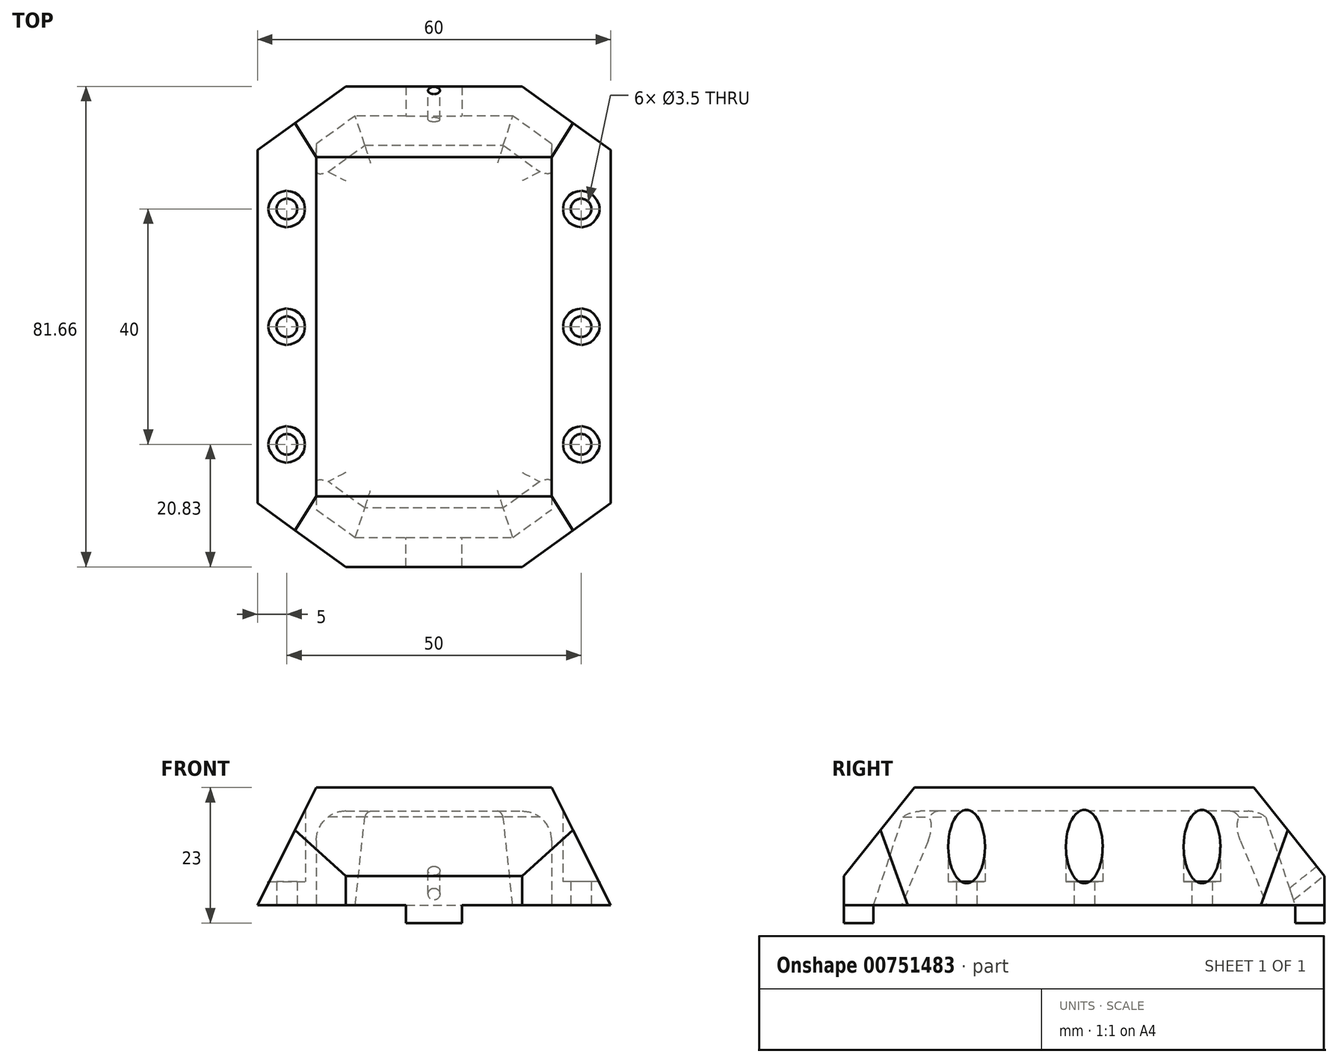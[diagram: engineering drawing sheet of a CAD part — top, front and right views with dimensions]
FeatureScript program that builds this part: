
annotation { "Feature Type Name" : "Feature", "Feature Type Description" : "" }
export const myFeature = defineFeature(function(context is Context, id is Id, definition is map)
    precondition{}
    {
        {
            var Q0;
            Q0=qCreatedBy(makeId("Top.planeOp"),FACE);
            var sketch = newSketch(context, id + "F0", { "sketchPlane" : qUnion([Q0])});
            skCircle(sketch, "E0", {"center": v(-25, 20) * mm, "radius": 1.75 * mm});
            skCircle(sketch, "E1", {"center": v(-25, 0) * mm, "radius": 1.75 * mm});
            skCircle(sketch, "E2", {"center": v(-25, -20) * mm, "radius": 1.75 * mm});
            skCircle(sketch, "E3", {"center": v(25, 20) * mm, "radius": 1.75 * mm});
            skCircle(sketch, "E4", {"center": v(25, 0) * mm, "radius": 1.75 * mm});
            skCircle(sketch, "E5", {"center": v(25, -20) * mm, "radius": 1.75 * mm});
            skLineSegment(sketch, "E6", {"start": v(-25, 0) * mm, "end": v(-25, 20) * mm, "construction": true});
            skLineSegment(sketch, "E7", {"start": v(-25, 0) * mm, "end": v(-25, -20) * mm, "construction": true});
            skLineSegment(sketch, "E8", {"start": v(-30, 30) * mm, "end": v(-30, -30) * mm});
            skPoint(sketch, "E9", {"position": v(-30, 0) * mm});
            skLineSegment(sketch, "E10", {"start": v(-30, 30) * mm, "end": v(-15, 40.83) * mm});
            skLineSegment(sketch, "E11.MirrorCS", {"start": v(-30, -30) * mm, "end": v(-15, -40.83) * mm});
            skLineSegment(sketch, "E12.MirrorCS", {"start": v(30, 30) * mm, "end": v(15, 40.83) * mm});
            skLineSegment(sketch, "E13.MirrorCS", {"start": v(30, 30) * mm, "end": v(30, -30) * mm});
            skLineSegment(sketch, "E14.MirrorCS", {"start": v(30, -30) * mm, "end": v(15, -40.83) * mm});
            skLineSegment(sketch, "E15", {"start": v(-15, 40.83) * mm, "end": v(15, 40.83) * mm});
            skLineSegment(sketch, "E16", {"start": v(-15, -40.83) * mm, "end": v(15, -40.83) * mm});
            skLineSegment(sketch, "E17.0", {"start": v(-20, -24.89) * mm, "end": v(-11.77, -30.83) * mm});
            skLineSegment(sketch, "E17.1", {"start": v(-20, 24.89) * mm, "end": v(-20, -24.89) * mm});
            skLineSegment(sketch, "E17.2", {"start": v(-11.77, -30.83) * mm, "end": v(11.77, -30.83) * mm});
            skLineSegment(sketch, "E17.3", {"start": v(-20, 24.89) * mm, "end": v(-11.77, 30.83) * mm});
            skLineSegment(sketch, "E17.4", {"start": v(20, -24.89) * mm, "end": v(11.77, -30.83) * mm});
            skLineSegment(sketch, "E17.5", {"start": v(20, 24.89) * mm, "end": v(20, -24.89) * mm});
            skLineSegment(sketch, "E17.6", {"start": v(20, 24.89) * mm, "end": v(11.77, 30.83) * mm});
            skLineSegment(sketch, "E17.7", {"start": v(-11.77, 30.83) * mm, "end": v(11.77, 30.83) * mm});
            skCircle(sketch, "E18", {"center": v(-25, -20) * mm, "radius": 3.12 * mm});
            skCircle(sketch, "E19", {"center": v(-25, 0) * mm, "radius": 3.12 * mm});
            skCircle(sketch, "E20", {"center": v(-25, 20) * mm, "radius": 3.12 * mm});
            skCircle(sketch, "E21.MirrorC", {"center": v(25, 20) * mm, "radius": 3.12 * mm});
            skCircle(sketch, "E22.MirrorC", {"center": v(25, 0) * mm, "radius": 3.12 * mm});
            skCircle(sketch, "E23.MirrorC", {"center": v(25, -20) * mm, "radius": 3.12 * mm});
            skSolve(sketch);
        }
        {
            var Q0;
            Q0=makeQuery(id+"F0.imprint","IMPRINT",FACE,{"disambiguationData":[TD([[makeQuery(id+"F0.imprint","IMPRINT",EDGE,{"derivedFrom":sQuery(id+"F0.wireOp",EDGE,"E8")}),1.0]])]});
            extrude(context, id + "F1", {"entities" : qUnion([Q0]), "depth" : 20 * mm, "offsetDistance" : 25 * mm});
        }
        {
            var Q0;
            Q0=makeQuery(id+"F0.imprint","IMPRINT",FACE,{"disambiguationData":[TD([[makeQuery(id+"F0.imprint","IMPRINT",EDGE,{"derivedFrom":sQuery(id+"F0.wireOp",EDGE,"E17.0")}),1.0]])]});
            extrude(context, id + "F2", {"entities" : qUnion([Q0]), "operationType" : NewBodyOperationType.ADD, "depth" : 20 * mm, "offsetDistance" : 25 * mm, "hasSecondDirection" : true, "secondDirectionOppositeDirection" : false, "secondDirectionDepth" : 16 * mm});
        }
        {
            var Q0;
            Q0=makeQuery(id+"F1.opExtrude","CAP_EDGE",EDGE,{"disambiguationData":[OSD([sQuery(id+"F0.wireOp",EDGE,"E8")])],"isStart":false});
            var Q1;
            Q1=makeQuery(id+"F1.opExtrude","CAP_EDGE",EDGE,{"disambiguationData":[OSD([sQuery(id+"F0.wireOp",EDGE,"E13.MirrorCS")])],"isStart":false});
            chamfer(context, id + "F3", {"entities" : qUnion([Q0, Q1]), "chamferType" : ChamferType.TWO_OFFSETS, "width1" : 10 * mm, "oppositeDirection" : false, "width2" : 20 * mm, "tangentPropagation" : true});
        }
        {
            var Q0;
            Q0=makeQuery(id+"F1.opExtrude","CAP_EDGE",EDGE,{"disambiguationData":[OSD([sQuery(id+"F0.wireOp",EDGE,"E16")])],"isStart":false});
            var Q1;
            Q1=makeQuery(id+"F1.opExtrude","CAP_EDGE",EDGE,{"disambiguationData":[OSD([sQuery(id+"F0.wireOp",EDGE,"E15")])],"isStart":false});
            chamfer(context, id + "F4", {"entities" : qUnion([Q0, Q1]), "chamferType" : ChamferType.TWO_OFFSETS, "width1" : 12 * mm, "oppositeDirection" : false, "width2" : 15 * mm, "tangentPropagation" : true});
        }
        {
            var Q0;
            Q0=makeQuery(id+"F0.imprint","IMPRINT",FACE,{"disambiguationData":[TD([[makeQuery(id+"F0.imprint","IMPRINT",EDGE,{"derivedFrom":sQuery(id+"F0.wireOp",EDGE,"E5")}),-1.0]])]});
            var Q1;
            Q1=makeQuery(id+"F0.imprint","IMPRINT",FACE,{"disambiguationData":[TD([[makeQuery(id+"F0.imprint","IMPRINT",EDGE,{"derivedFrom":sQuery(id+"F0.wireOp",EDGE,"E4")}),-1.0]])]});
            var Q2;
            Q2=makeQuery(id+"F0.imprint","IMPRINT",FACE,{"disambiguationData":[TD([[makeQuery(id+"F0.imprint","IMPRINT",EDGE,{"derivedFrom":sQuery(id+"F0.wireOp",EDGE,"E3")}),-1.0]])]});
            var Q3;
            Q3=makeQuery(id+"F0.imprint","IMPRINT",FACE,{"disambiguationData":[TD([[makeQuery(id+"F0.imprint","IMPRINT",EDGE,{"derivedFrom":sQuery(id+"F0.wireOp",EDGE,"E2")}),-1.0]])]});
            var Q4;
            Q4=makeQuery(id+"F0.imprint","IMPRINT",FACE,{"disambiguationData":[TD([[makeQuery(id+"F0.imprint","IMPRINT",EDGE,{"derivedFrom":sQuery(id+"F0.wireOp",EDGE,"E1")}),-1.0]])]});
            var Q5;
            Q5=makeQuery(id+"F0.imprint","IMPRINT",FACE,{"disambiguationData":[TD([[makeQuery(id+"F0.imprint","IMPRINT",EDGE,{"derivedFrom":sQuery(id+"F0.wireOp",EDGE,"E0")}),-1.0]])]});
            extrude(context, id + "F5", {"entities" : qUnion([Q0, Q1, Q2, Q3, Q4, Q5]), "operationType" : NewBodyOperationType.ADD, "depth" : 4 * mm, "offsetDistance" : 25 * mm});
        }
        {
            var Q0;
            Q0=makeQuery(id+"F1.opExtrude","CAP_EDGE",EDGE,{"disambiguationData":[OSD([sQuery(id+"F0.wireOp",EDGE,"E17.7")])],"isStart":true});
            var Q1;
            Q1=makeQuery(id+"F1.opExtrude","CAP_EDGE",EDGE,{"disambiguationData":[OSD([sQuery(id+"F0.wireOp",EDGE,"E17.3")])],"isStart":true});
            var Q2;
            Q2=makeQuery(id+"F1.opExtrude","CAP_EDGE",EDGE,{"disambiguationData":[OSD([sQuery(id+"F0.wireOp",EDGE,"E17.6")])],"isStart":true});
            var Q3;
            Q3=makeQuery(id+"F1.opExtrude","CAP_EDGE",EDGE,{"disambiguationData":[OSD([sQuery(id+"F0.wireOp",EDGE,"E17.2")])],"isStart":true});
            var Q4;
            Q4=makeQuery(id+"F1.opExtrude","CAP_EDGE",EDGE,{"disambiguationData":[OSD([sQuery(id+"F0.wireOp",EDGE,"E17.0")])],"isStart":true});
            var Q5;
            Q5=makeQuery(id+"F1.opExtrude","CAP_EDGE",EDGE,{"disambiguationData":[OSD([sQuery(id+"F0.wireOp",EDGE,"E17.4")])],"isStart":true});
            chamfer(context, id + "F6", {"entities" : qUnion([Q0, Q1, Q2, Q3, Q4, Q5]), "chamferType" : ChamferType.TWO_OFFSETS, "width1" : 15 * mm, "oppositeDirection" : false, "width2" : 5 * mm, "tangentPropagation" : true});
        }
        {
            var Q0;
            Q0=makeQuery(id+"F2.opExtrude","CAP_FACE",FACE,{"disambiguationData":[OSD([sQuery(id+"F0.wireOp",EDGE,"E17.0"),sQuery(id+"F0.wireOp",EDGE,"E17.1"),sQuery(id+"F0.wireOp",EDGE,"E17.2"),sQuery(id+"F0.wireOp",EDGE,"E17.3"),sQuery(id+"F0.wireOp",EDGE,"E17.4"),sQuery(id+"F0.wireOp",EDGE,"E17.5"),sQuery(id+"F0.wireOp",EDGE,"E17.6"),sQuery(id+"F0.wireOp",EDGE,"E17.7")])],"isStart":true});
            fillet(context, id + "F7", {"entities" : qUnion([Q0]), "radius" : 5 * mm, "tangentPropagation" : true, "allowEdgeOverflow" : false});
        }
        {
            var Q0;
            Q0=makeQuery(id+"F4.opChamfer","BLEND_FACE",FACE,{"disambiguationData":[OSD([sQuery(id+"F0.wireOp",EDGE,"E15")])]});
            var sketch = newSketch(context, id + "F8", { "sketchPlane" : qUnion([Q0])});
            skCircle(sketch, "E24", {"center": v(0, -20.5) * mm, "radius": 1 * mm});
            skPoint(sketch, "E24.centerSnap0", {"position": v(0, -25.5) * mm});
            skSolve(sketch);
        }
        {
            var Q0;
            {var subQ0=sQuery(id+"F8.wireOp",EDGE,"E24");var subQ1=sQuery(id+"F0.wireOp",EDGE,"E15");var subQ2=makeQuery(id+"F4.opChamfer","BLEND_EDGE",EDGE,{"blendedFrom":[makeQuery(id+"F1.opExtrude","CAP_EDGE",EDGE,{"disambiguationData":[OSD([subQ1])],"isStart":false}),makeQuery(id+"F1.opExtrude","SWEPT_FACE",FACE,{"disambiguationData":[OSD([subQ1])]})],"blendedInto":[makeQuery(id+"F1.opExtrude","SWEPT_FACE",FACE,{"disambiguationData":[OSD([subQ1])]})]});var subQ3=makeQuery(id+"F8.imprint","INTERSECT",VERTEX,{"disambiguationData":[OD(0.0)],"derivedFrom":[subQ2,subQ0]});Q0=makeQuery(id+"F8.imprint","IMPRINT",FACE,{"disambiguationData":[TD([[makeQuery(id+"F8.imprint","IMPRINT",EDGE,{"disambiguationData":[TD([[subQ3,-1.0]])],"derivedFrom":subQ0}),1.0]])]});}
            var Q1;
            {var subQ0=sQuery(id+"F8.wireOp",EDGE,"E24");var subQ1=sQuery(id+"F0.wireOp",EDGE,"E15");var subQ2=makeQuery(id+"F4.opChamfer","BLEND_EDGE",EDGE,{"blendedFrom":[makeQuery(id+"F1.opExtrude","CAP_EDGE",EDGE,{"disambiguationData":[OSD([subQ1])],"isStart":false}),makeQuery(id+"F1.opExtrude","SWEPT_FACE",FACE,{"disambiguationData":[OSD([subQ1])]})],"blendedInto":[makeQuery(id+"F1.opExtrude","SWEPT_FACE",FACE,{"disambiguationData":[OSD([subQ1])]})]});var subQ3=makeQuery(id+"F8.imprint","INTERSECT",VERTEX,{"disambiguationData":[OD(0.0)],"derivedFrom":[subQ2,subQ0]});Q1=makeQuery(id+"F8.imprint","IMPRINT",FACE,{"disambiguationData":[TD([[makeQuery(id+"F8.imprint","IMPRINT",EDGE,{"disambiguationData":[TD([[subQ3,1.0]])],"derivedFrom":subQ0}),1.0]])]});}
            var Q2;
            Q2=makeQuery(id+"F6.opChamfer","BLEND_FACE",FACE,{"disambiguationData":[OSD([sQuery(id+"F0.wireOp",EDGE,"E17.7")])]});
            extrude(context, id + "F9", {"entities" : qUnion([Q0, Q1]), "operationType" : NewBodyOperationType.REMOVE, "endBound" : BoundingType.UP_TO_SURFACE, "oppositeDirection" : true, "depth" : 25 * mm, "endBoundEntityFace" : qUnion([Q2]), "offsetDistance" : 25 * mm});
        }
        {
            var Q0;
            Q0=qCreatedBy(makeId("Top.planeOp"),FACE);
            var sketch = newSketch(context, id + "F10", { "sketchPlane" : qUnion([Q0])});
            skLineSegment(sketch, "E25.bottom", {"start": v(-4.75, -40.83) * mm, "end": v(4.75, -40.83) * mm});
            skLineSegment(sketch, "E25.top", {"start": v(-4.75, -35.83) * mm, "end": v(4.75, -35.83) * mm});
            skLineSegment(sketch, "E25.left", {"start": v(-4.75, -40.83) * mm, "end": v(-4.75, -35.83) * mm});
            skLineSegment(sketch, "E25.right", {"start": v(4.75, -40.83) * mm, "end": v(4.75, -35.83) * mm});
            skLineSegment(sketch, "E26.MirrorCS", {"start": v(-4.75, 35.83) * mm, "end": v(4.75, 35.83) * mm});
            skLineSegment(sketch, "E27.MirrorCS", {"start": v(4.75, 40.83) * mm, "end": v(4.75, 35.83) * mm});
            skLineSegment(sketch, "E28.MirrorCS", {"start": v(-4.75, 40.83) * mm, "end": v(4.75, 40.83) * mm});
            skLineSegment(sketch, "E29.MirrorCS", {"start": v(-4.75, 40.83) * mm, "end": v(-4.75, 35.83) * mm});
            skSolve(sketch);
        }
        {
            var Q0;
            Q0=makeQuery(id+"F10.imprint","IMPRINT",FACE,{"disambiguationData":[TD([[makeQuery(id+"F10.imprint","IMPRINT",EDGE,{"derivedFrom":sQuery(id+"F10.wireOp",EDGE,"E25.bottom")}),1.0]])]});
            var Q1;
            Q1=makeQuery(id+"F10.imprint","IMPRINT",FACE,{"disambiguationData":[TD([[makeQuery(id+"F10.imprint","IMPRINT",EDGE,{"derivedFrom":sQuery(id+"F10.wireOp",EDGE,"E26.MirrorCS")}),1.0]])]});
            extrude(context, id + "F11", {"entities" : qUnion([Q0, Q1]), "operationType" : NewBodyOperationType.ADD, "oppositeDirection" : true, "depth" : 3 * mm, "offsetDistance" : 25 * mm});
        }
    });
